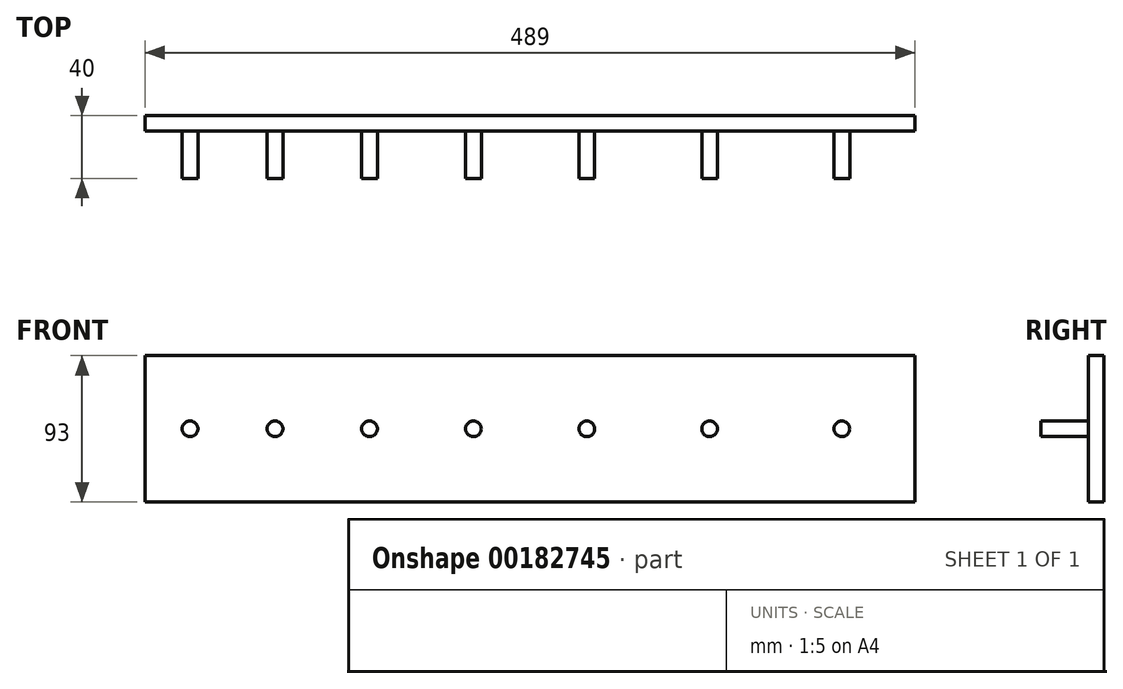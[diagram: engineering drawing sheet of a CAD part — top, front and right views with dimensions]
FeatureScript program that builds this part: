
annotation { "Feature Type Name" : "Feature", "Feature Type Description" : "" }
export const myFeature = defineFeature(function(context is Context, id is Id, definition is map)
    precondition{}
    {
        {
            assignVariable(context, id + "F0", {"name" : "t", "anyValue" : 3});
        }
        {
            var Q0;
            Q0=qCreatedBy(makeId("Front.planeOp"),FACE);
            var sketch = newSketch(context, id + "F1", { "sketchPlane" : qUnion([Q0])});
            skLineSegment(sketch, "E0.bottom", {"start": v(-28.5, 46.5) * mm, "end": v(460.5, 46.5) * mm});
            skLineSegment(sketch, "E0.top", {"start": v(-28.5, -46.5) * mm, "end": v(460.5, -46.5) * mm});
            skLineSegment(sketch, "E0.left", {"start": v(-28.5, 46.5) * mm, "end": v(-28.5, -46.5) * mm});
            skLineSegment(sketch, "E0.right", {"start": v(460.5, 46.5) * mm, "end": v(460.5, -46.5) * mm});
            skPoint(sketch, "E1.0", {"position": v(0, 0) * mm});
            skSolve(sketch);
        }
        {
            var Q0;
            Q0=makeQuery(id+"F1.imprint","IMPRINT",FACE,{"disambiguationData":[TD([[makeQuery(id+"F1.imprint","IMPRINT",EDGE,{"derivedFrom":sQuery(id+"F1.wireOp",EDGE,"E0.bottom")}),-1.0]])]});
            extrude(context, id + "F2", {"entities" : qUnion([Q0]), "depth" : 10 * mm});
        }
        {
            var Q0;
            Q0=makeQuery(id+"F2.opExtrude","CAP_FACE",FACE,{"disambiguationData":[OSD([sQuery(id+"F1.wireOp",EDGE,"E0.bottom"),sQuery(id+"F1.wireOp",EDGE,"E0.top"),sQuery(id+"F1.wireOp",EDGE,"E0.left"),sQuery(id+"F1.wireOp",EDGE,"E0.right")])],"isStart":false});
            var sketch = newSketch(context, id + "F3", { "sketchPlane" : qUnion([Q0])});
            skCircle(sketch, "E2", {"center": v(0, 0) * mm, "radius": 5 * mm});
            skCircle(sketch, "E3", {"center": v(54, 0) * mm, "radius": 5 * mm});
            skCircle(sketch, "E4", {"center": v(114, 0) * mm, "radius": 5 * mm});
            skCircle(sketch, "E5", {"center": v(180, 0) * mm, "radius": 5 * mm});
            skCircle(sketch, "E6", {"center": v(252, 0) * mm, "radius": 5 * mm});
            skCircle(sketch, "E7", {"center": v(330, 0) * mm, "radius": 5 * mm});
            skCircle(sketch, "E8", {"center": v(414, 0) * mm, "radius": 5 * mm});
            skSolve(sketch);
        }
        {
            var Q0;
            Q0=makeQuery(id+"F3.imprint","IMPRINT",FACE,{"disambiguationData":[TD([[makeQuery(id+"F3.imprint","IMPRINT",EDGE,{"derivedFrom":sQuery(id+"F3.wireOp",EDGE,"E2")}),1.0]])]});
            var Q1;
            Q1=makeQuery(id+"F3.imprint","IMPRINT",FACE,{"disambiguationData":[TD([[makeQuery(id+"F3.imprint","IMPRINT",EDGE,{"derivedFrom":sQuery(id+"F3.wireOp",EDGE,"E3")}),1.0]])]});
            var Q2;
            Q2=makeQuery(id+"F3.imprint","IMPRINT",FACE,{"disambiguationData":[TD([[makeQuery(id+"F3.imprint","IMPRINT",EDGE,{"derivedFrom":sQuery(id+"F3.wireOp",EDGE,"E4")}),1.0]])]});
            var Q3;
            Q3=makeQuery(id+"F3.imprint","IMPRINT",FACE,{"disambiguationData":[TD([[makeQuery(id+"F3.imprint","IMPRINT",EDGE,{"derivedFrom":sQuery(id+"F3.wireOp",EDGE,"E5")}),1.0]])]});
            var Q4;
            Q4=makeQuery(id+"F3.imprint","IMPRINT",FACE,{"disambiguationData":[TD([[makeQuery(id+"F3.imprint","IMPRINT",EDGE,{"derivedFrom":sQuery(id+"F3.wireOp",EDGE,"E6")}),1.0]])]});
            var Q5;
            Q5=makeQuery(id+"F3.imprint","IMPRINT",FACE,{"disambiguationData":[TD([[makeQuery(id+"F3.imprint","IMPRINT",EDGE,{"derivedFrom":sQuery(id+"F3.wireOp",EDGE,"E7")}),1.0]])]});
            var Q6;
            Q6=makeQuery(id+"F3.imprint","IMPRINT",FACE,{"disambiguationData":[TD([[makeQuery(id+"F3.imprint","IMPRINT",EDGE,{"derivedFrom":sQuery(id+"F3.wireOp",EDGE,"E8")}),1.0]])]});
            extrude(context, id + "F4", {"entities" : qUnion([Q0, Q1, Q2, Q3, Q4, Q5, Q6]), "operationType" : NewBodyOperationType.ADD, "depth" : (getVariable(context, 't') * 10) * mm});
        }
    });
